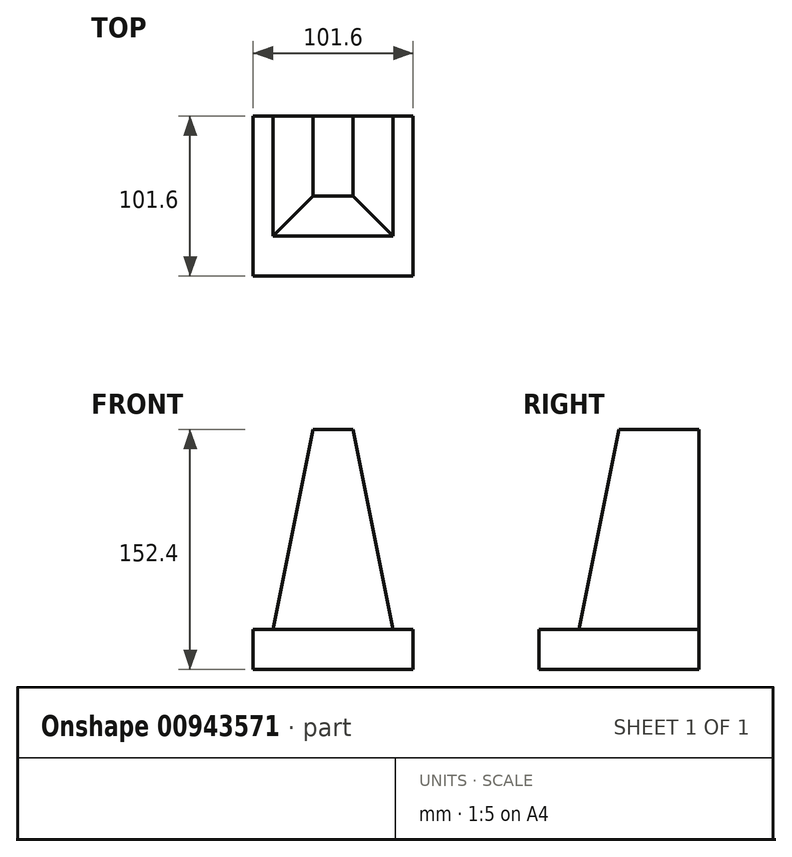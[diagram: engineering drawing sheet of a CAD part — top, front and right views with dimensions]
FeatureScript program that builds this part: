
annotation { "Feature Type Name" : "Feature", "Feature Type Description" : "" }
export const myFeature = defineFeature(function(context is Context, id is Id, definition is map)
    precondition{}
    {
        {
            var Q0;
            Q0=qCreatedBy(makeId("Top.planeOp"),FACE);
            var sketch = newSketch(context, id + "F0", { "sketchPlane" : qUnion([Q0])});
            skLineSegment(sketch, "E0.bottom", {"start": v(0, 0) * mm, "end": v(101.6, 0) * mm});
            skLineSegment(sketch, "E0.top", {"start": v(0, 101.6) * mm, "end": v(101.6, 101.6) * mm});
            skLineSegment(sketch, "E0.left", {"start": v(0, 0) * mm, "end": v(0, 101.6) * mm});
            skLineSegment(sketch, "E0.right", {"start": v(101.6, 0) * mm, "end": v(101.6, 101.6) * mm});
            skSolve(sketch);
        }
        {
            var Q0;
            Q0 = qSketchRegion(id + "F0", true);
            extrude(context, id + "F1", {"entities" : qUnion([Q0]), "depth" : 25.4 * mm, "offsetDistance" : 25.4 * mm});
        }
        {
            var Q0;
            Q0=makeQuery(id+"F1.opExtrude","CAP_FACE",FACE,{"disambiguationData":[OSD([sQuery(id+"F0.wireOp",EDGE,"E0.bottom"),sQuery(id+"F0.wireOp",EDGE,"E0.top"),sQuery(id+"F0.wireOp",EDGE,"E0.left"),sQuery(id+"F0.wireOp",EDGE,"E0.right")])],"isStart":false});
            var sketch = newSketch(context, id + "F2", { "sketchPlane" : qUnion([Q0])});
            skLineSegment(sketch, "E1.bottom", {"start": v(12.7, 25.4) * mm, "end": v(88.9, 25.4) * mm});
            skLineSegment(sketch, "E1.top", {"start": v(12.7, 101.6) * mm, "end": v(88.9, 101.6) * mm});
            skLineSegment(sketch, "E1.left", {"start": v(12.7, 25.4) * mm, "end": v(12.7, 101.6) * mm});
            skLineSegment(sketch, "E1.right", {"start": v(88.9, 25.4) * mm, "end": v(88.9, 101.6) * mm});
            skSolve(sketch);
        }
        {
            var Q0;
            Q0=qCreatedBy(makeId("Top.planeOp"),FACE);
            cPlane(context, id + "F3", {"entities" : qUnion([Q0]), "cplaneType" : CPlaneType.OFFSET, "offset" : 152.4 * mm, "width" : 152.4 * mm, "height" : 152.4 * mm});
        }
        {
            var Q0;
            Q0=qCreatedBy(id+"F3.planeOp",FACE);
            var sketch = newSketch(context, id + "F4", { "sketchPlane" : qUnion([Q0])});
            skLineSegment(sketch, "E2.bottom", {"start": v(38.1, 50.8) * mm, "end": v(63.5, 50.8) * mm});
            skLineSegment(sketch, "E2.top", {"start": v(38.1, 101.6) * mm, "end": v(63.5, 101.6) * mm});
            skLineSegment(sketch, "E2.left", {"start": v(38.1, 50.8) * mm, "end": v(38.1, 101.6) * mm});
            skLineSegment(sketch, "E2.right", {"start": v(63.5, 50.8) * mm, "end": v(63.5, 101.6) * mm});
            skSolve(sketch);
        }
        {
            var Q1;
            Q1=makeQuery(id+"F4.imprint","IMPRINT",FACE,{"disambiguationData":[TD([[makeQuery(id+"F4.imprint","IMPRINT",EDGE,{"derivedFrom":sQuery(id+"F4.wireOp",EDGE,"E2.bottom")}),1.0]])]});
            var Q2;
            Q2=makeQuery(id+"F2.imprint","IMPRINT",FACE,{"disambiguationData":[TD([[makeQuery(id+"F2.imprint","IMPRINT",EDGE,{"derivedFrom":sQuery(id+"F2.wireOp",EDGE,"E1.bottom")}),1.0]])]});
            loft(context, id + "F5", {"operationType" : NewBodyOperationType.ADD, "sheetProfilesArray" : [{ "sheetProfileEntities" : qUnion([Q1]) }, { "sheetProfileEntities" : qUnion([Q2]) }]});
        }
    });
